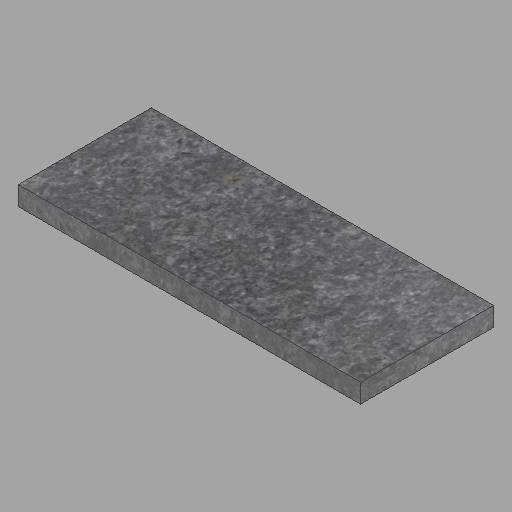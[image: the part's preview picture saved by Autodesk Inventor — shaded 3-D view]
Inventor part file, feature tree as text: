
AUTODESK INVENTOR PART (.ipt)
format: ipt  version: 2023 (Build 270158000, 158)  size: 222,208 bytes
history: native  units: in
note: dims shown in document units (in); Inventor stores cm internally (conversion verified against a paired STEP export)
features: other x1, extrude x1, sketch x1
ambient origin geometry x8: Origin, YZ Plane, XZ Plane, XY Plane, X Axis, Y Axis, Z Axis, Center Point
bodies: Solid1 (feature_tree)
feature tree (3):
  other  "2x14x36-18"
  extrude  "Extrusion1"  Depth=14.0in
  sketch  "Sketch1"  dims[d0=2.0in d1=14.0in d2=36.0in d3=0.0in]
